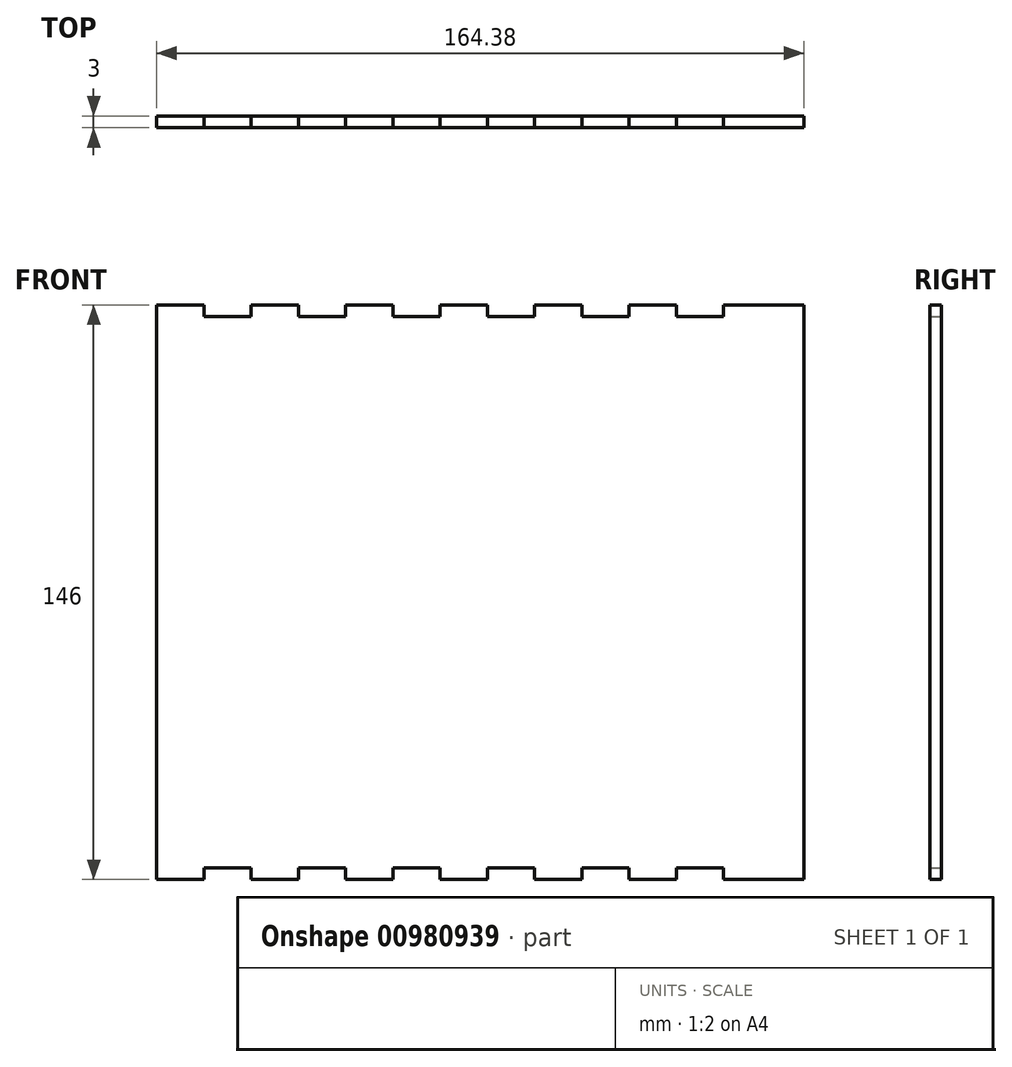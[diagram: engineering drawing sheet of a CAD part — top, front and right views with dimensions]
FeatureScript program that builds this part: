
annotation { "Feature Type Name" : "Feature", "Feature Type Description" : "" }
export const myFeature = defineFeature(function(context is Context, id is Id, definition is map)
    precondition{}
    {
        {
            var Q0;
            Q0=qCreatedBy(makeId("Front.planeOp"),FACE);
            var sketch = newSketch(context, id + "F0", { "sketchPlane" : qUnion([Q0])});
            skPoint(sketch, "E0.middle", {"position": v(0, 0) * mm});
            skLineSegment(sketch, "E1", {"start": v(-78, 73) * mm, "end": v(-66, 73) * mm});
            skLineSegment(sketch, "E2", {"start": v(-66, 73) * mm, "end": v(-66, 70) * mm});
            skLineSegment(sketch, "E3", {"start": v(-66, 70) * mm, "end": v(-54, 70) * mm});
            skLineSegment(sketch, "E4", {"start": v(-54, 70) * mm, "end": v(-54, 73) * mm});
            skLineSegment(sketch, "E5", {"start": v(-54, 73) * mm, "end": v(-42, 73) * mm});
            skLineSegment(sketch, "E6.1.0.0", {"start": v(-42, 70) * mm, "end": v(-30, 70) * mm});
            skLineSegment(sketch, "E6.1.0.1", {"start": v(-30, 73) * mm, "end": v(-18, 73) * mm});
            skLineSegment(sketch, "E6.1.0.3", {"start": v(-42, 73) * mm, "end": v(-42, 70) * mm});
            skLineSegment(sketch, "E6.1.0.4", {"start": v(-30, 70) * mm, "end": v(-30, 73) * mm});
            skLineSegment(sketch, "E6.2.0.0", {"start": v(-18, 70) * mm, "end": v(-6, 70) * mm});
            skLineSegment(sketch, "E6.2.0.1", {"start": v(-6, 73) * mm, "end": v(6, 73) * mm});
            skLineSegment(sketch, "E6.2.0.2", {"start": v(-30, 73) * mm, "end": v(-18, 73) * mm});
            skLineSegment(sketch, "E6.2.0.3", {"start": v(-18, 73) * mm, "end": v(-18, 70) * mm});
            skLineSegment(sketch, "E6.2.0.4", {"start": v(-6, 70) * mm, "end": v(-6, 73) * mm});
            skLineSegment(sketch, "E6.3.0.0", {"start": v(6, 70) * mm, "end": v(18, 70) * mm});
            skLineSegment(sketch, "E6.3.0.1", {"start": v(18, 73) * mm, "end": v(30, 73) * mm});
            skLineSegment(sketch, "E6.3.0.2", {"start": v(-6, 73) * mm, "end": v(6, 73) * mm});
            skLineSegment(sketch, "E6.3.0.3", {"start": v(6, 73) * mm, "end": v(6, 70) * mm});
            skLineSegment(sketch, "E6.3.0.4", {"start": v(18, 70) * mm, "end": v(18, 73) * mm});
            skLineSegment(sketch, "E6.4.0.0", {"start": v(30, 70) * mm, "end": v(42, 70) * mm});
            skLineSegment(sketch, "E6.4.0.1", {"start": v(42, 73) * mm, "end": v(54, 73) * mm});
            skLineSegment(sketch, "E6.4.0.2", {"start": v(18, 73) * mm, "end": v(30, 73) * mm});
            skLineSegment(sketch, "E6.4.0.3", {"start": v(30, 73) * mm, "end": v(30, 70) * mm});
            skLineSegment(sketch, "E6.4.0.4", {"start": v(42, 70) * mm, "end": v(42, 73) * mm});
            skLineSegment(sketch, "E6.5.0.0", {"start": v(54, 70) * mm, "end": v(66, 70) * mm});
            skLineSegment(sketch, "E6.5.0.2", {"start": v(42, 73) * mm, "end": v(54, 73) * mm});
            skLineSegment(sketch, "E6.5.0.3", {"start": v(54, 73) * mm, "end": v(54, 70) * mm});
            skLineSegment(sketch, "E6.5.0.4", {"start": v(66, 70) * mm, "end": v(66, 73) * mm});
            skLineSegment(sketch, "E6.direction1", {"start": v(-78, 73) * mm, "end": v(-54, 73) * mm, "construction": true});
            skLineSegment(sketch, "E7.MirrorCS", {"start": v(-54, -70) * mm, "end": v(-54, -73) * mm});
            skLineSegment(sketch, "E8.MirrorCS", {"start": v(-6, -70) * mm, "end": v(-6, -73) * mm});
            skLineSegment(sketch, "E9.MirrorCS", {"start": v(18, -70) * mm, "end": v(18, -73) * mm});
            skLineSegment(sketch, "E10.MirrorCS", {"start": v(42, -70) * mm, "end": v(42, -73) * mm});
            skLineSegment(sketch, "E11.MirrorCS", {"start": v(6, -73) * mm, "end": v(6, -70) * mm});
            skLineSegment(sketch, "E12.MirrorCS", {"start": v(-30, -70) * mm, "end": v(-30, -73) * mm});
            skLineSegment(sketch, "E13.MirrorCS", {"start": v(-42, -73) * mm, "end": v(-42, -70) * mm});
            skLineSegment(sketch, "E14.MirrorCS", {"start": v(54, -73) * mm, "end": v(54, -70) * mm});
            skLineSegment(sketch, "E15.MirrorCS", {"start": v(30, -73) * mm, "end": v(30, -70) * mm});
            skLineSegment(sketch, "E16.MirrorCS", {"start": v(-18, -73) * mm, "end": v(-18, -70) * mm});
            skLineSegment(sketch, "E17.MirrorCS", {"start": v(66, -70) * mm, "end": v(66, -73) * mm});
            skLineSegment(sketch, "E18.MirrorCS", {"start": v(-66, -73) * mm, "end": v(-66, -70) * mm});
            skLineSegment(sketch, "E19.MirrorCS", {"start": v(-54, -73) * mm, "end": v(-42, -73) * mm});
            skLineSegment(sketch, "E20.MirrorCS", {"start": v(42, -73) * mm, "end": v(54, -73) * mm});
            skLineSegment(sketch, "E21.MirrorCS", {"start": v(-30, -73) * mm, "end": v(-18, -73) * mm});
            skLineSegment(sketch, "E22.MirrorCS", {"start": v(-6, -73) * mm, "end": v(6, -73) * mm});
            skLineSegment(sketch, "E23.MirrorCS", {"start": v(18, -73) * mm, "end": v(30, -73) * mm});
            skLineSegment(sketch, "E24.MirrorCS", {"start": v(-78, -73) * mm, "end": v(-66, -73) * mm});
            skLineSegment(sketch, "E25.MirrorCS", {"start": v(-18, -70) * mm, "end": v(-6, -70) * mm});
            skLineSegment(sketch, "E26.MirrorCS", {"start": v(-66, -70) * mm, "end": v(-54, -70) * mm});
            skLineSegment(sketch, "E27.MirrorCS", {"start": v(54, -70) * mm, "end": v(66, -70) * mm});
            skLineSegment(sketch, "E28.MirrorCS", {"start": v(-78, -73) * mm, "end": v(-54, -73) * mm, "construction": true});
            skLineSegment(sketch, "E29.MirrorCS", {"start": v(-42, -70) * mm, "end": v(-30, -70) * mm});
            skLineSegment(sketch, "E30.MirrorCS", {"start": v(6, -70) * mm, "end": v(18, -70) * mm});
            skLineSegment(sketch, "E31.MirrorCS", {"start": v(30, -70) * mm, "end": v(42, -70) * mm});
            skLineSegment(sketch, "E32.5.0.2", {"start": v(-78, 73) * mm, "end": v(-78, 73) * mm});
            skLineSegment(sketch, "E32.direction1", {"start": v(-78, -61.77) * mm, "end": v(-78, -50.54) * mm, "construction": true});
            skLineSegment(sketch, "E33", {"start": v(66, 73) * mm, "end": v(86.38, 73) * mm});
            skLineSegment(sketch, "E34", {"start": v(66, -73) * mm, "end": v(86.38, -73) * mm});
            skLineSegment(sketch, "E35", {"start": v(-78, 73) * mm, "end": v(-78, -73) * mm});
            skLineSegment(sketch, "E36", {"start": v(86.38, 73) * mm, "end": v(86.38, -73) * mm});
            skPoint(sketch, "E37.orphan", {"position": v(90, -73) * mm});
            skSolve(sketch);
        }
        {
            var Q0;
            {var subQ0=sQuery(id+"F0.wireOp",EDGE,"E1");Q0=makeQuery(id+"F0.imprint","IMPRINT",FACE,{"disambiguationData":[TD([[makeQuery(id+"F0.imprint","IMPRINT",EDGE,{"derivedFrom":subQ0}),-1.0]])]});}
            extrude(context, id + "F1", {"entities" : qUnion([Q0]), "depth" : 3 * mm, "offsetDistance" : 25 * mm});
        }
    });
